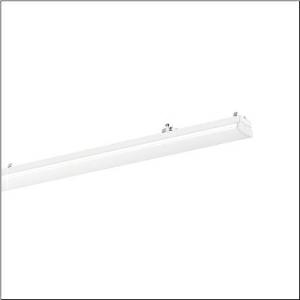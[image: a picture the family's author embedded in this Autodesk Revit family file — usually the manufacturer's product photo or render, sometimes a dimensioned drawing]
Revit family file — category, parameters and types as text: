
# Revit family: licross_r__11_recessed_opal_mo_51te1ddn445g_55f5
name_source: partatom
category: Lighting Fixtures
units: mm (PartAtom-declared; Revit-internal decimal feet)

## family parameters
Cut with Voids When Loaded = No
Host = Face
Light Source = No
Part Type = Normal
Room Calculation Point = No
Round Connector Dimension = Use Diameter
Shared = No

## types (1)
- --- (1 x LED, 4500 lm, 25.2 W, 4000K)
    Apparent Load = 25 VA
    CIE Flux Codes = 44 73 91 87 100
    Color Rendering = 80
    Color Temperature = 4000K
    Default Elevation = 1800 mm
    Description = Licross® 11 recessed opal MO, luminaire insert, of sheet steel, coil coated, white, length: 1.500mm, width: 76mm, height: 87mm, LED rated luminous flux: 4.500lm, light colour: 840, control gear: DALI 2, with plug, 5-pole, with phase selection, mains connection: 220..240V, AC, 50/60Hz, rated input power: 25W, internal wiring halogen-free, primary optical cover: cover, of PMMA, light emission: direct with ceiling illumination distribution, primary light characteristic: symmetric, protection rating (complete): IP54, insulation class (complete): insulation class I (protective earthing), certification: CE, ENEC, VDE, UKCA, protection symbol: D if used in an environment with non-conductive dust loads with corresponding accessories, impact resistance: IK06, permissible ambient temperature for indoor applications: -25..+45°C, corresponds to IFS (International Featured Standards) requirements for safety and quality in the food industry, reducing of maximum allowable ambient temperature of 5°C with ceiling mounting, LABS conformity tested according to VDMA 24364:2018-05, packaging unit: 1 piece
    Height = 83 mm
    Lamp = 1 x LED
    Lamp Light Flux = 4500 lm
    Lamp Power = 25.2 W
    Lamp count = 1
    Length = 1500 mm
    Luminous efficacy = 179 lm/W
    Manufacturer = Siteco
    ModVariant = No
    Model = 51TE1DDN445G
    Mounting Place = Ceiling
    Mounting Type = Pendant
    Number of Poles = 1
    OnlyDefault = Yes
    Power Factor = 1
    Product Name = Licross® 11 recessed opal MO
    Product group = luminaire insert | ceiling pendant
    ProductGroupID = 902
    Protection Class = Protection class I
    Protection Degree = IP 54
    RLX_Detail_Level = 1
    RLX_Emergency_Light_Flux = 0 lm
    RLX_Emergency_Type = 0
    RLX_Emergency_Type_DB = No
    RlxData = <blob elided: 26701 chars, md5=375e5e6f>
    Socket = socket
    Standby Power = 0 W
    System Light Flux = 4500 lm
    System Power = 25 W
    Type Comments = factory setting: luminous flux: 100 % | dim-lin: 254 | 167 mA
    Type Image = l_1313666.jpg
    URL = http://relux.com
    VarID = @adj_097551
    Voltage = 0 V
    Weight = 0.00 kg
    Width = 76 mm

## geometry (parser evidence)
native form markers: Blend x4, Sweep x15
no freeform markers — native parametric forms only
